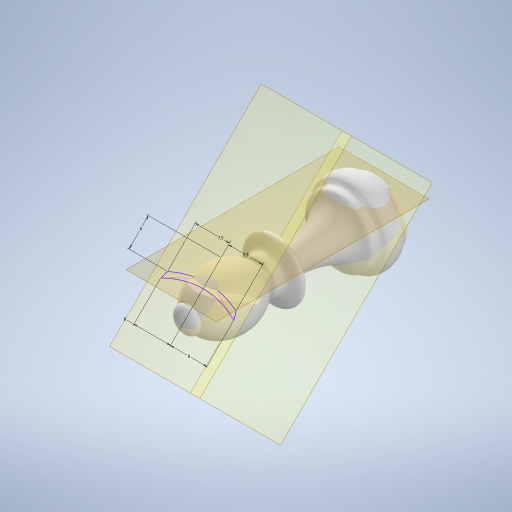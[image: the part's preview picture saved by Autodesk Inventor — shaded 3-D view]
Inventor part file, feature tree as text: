
AUTODESK INVENTOR PART (.ipt)
format: ipt  version: 2024.1 (Build 281209000, 209)  size: 571,904 bytes
history: native  units: mm
features: sketch x5, plane x3, extrude x2, other x1, revolve x1, fillet x1, sweep x1, projected_geometry x1
ambient origin geometry x8: Origin, YZ Plane, XZ Plane, XY Plane, X Axis, Y Axis, Z Axis, Center Point
bodies: Solid1 (feature_tree)
feature tree (15):
  extrude  "Extrusion1"  Depth=3.0mm TaperAngle=0.0deg
  other  "Work Axis1"
  extrude  "Extrusion2"  Depth=14.3mm
  revolve  "Revolution1"  [1 undecoded]
  fillet  "Fillet5"  Radius=0.6mm
  plane  "Work Plane6"
  plane  "Work Plane9"
  sweep  "Sweep1"
  sketch  "Sketch1"  dims[d0=10.0mm d1=3.0mm d2=0.0mm]
  sketch  "Sketch2"  dims[d5=360.0deg d6=14.3mm]
  sketch  "Sketch3"  dims[d7=3.0mm d8=0.0mm d89=12.3mm d107=0.6mm]
  projected_geometry  "Projected Loop1"
  plane  "Work Plane7"
  sketch  "Sketch16"  dims[d127=2.8mm d128=1.4mm]
  sketch  "Sketch17"  dims[d129=6.3mm d130=8.0mm d131=8.0mm d132=33.0mm d133=11.2mm d134=6.75mm d135=0.8mm d136=25.0mm d137=8.0mm d138=8.0mm d141=6.0mm d142=7.5mm d143=7.5mm d144=0.0mm d145=0.0mm d98=0.0mm d99=0.0mm d100=0.0mm d101=0.0mm]
note: 1 required parameter value undecoded (feature->parameter linkage not recoverable at this tier; creation-order binding heuristic only, values carry confidence <= 0.55)
